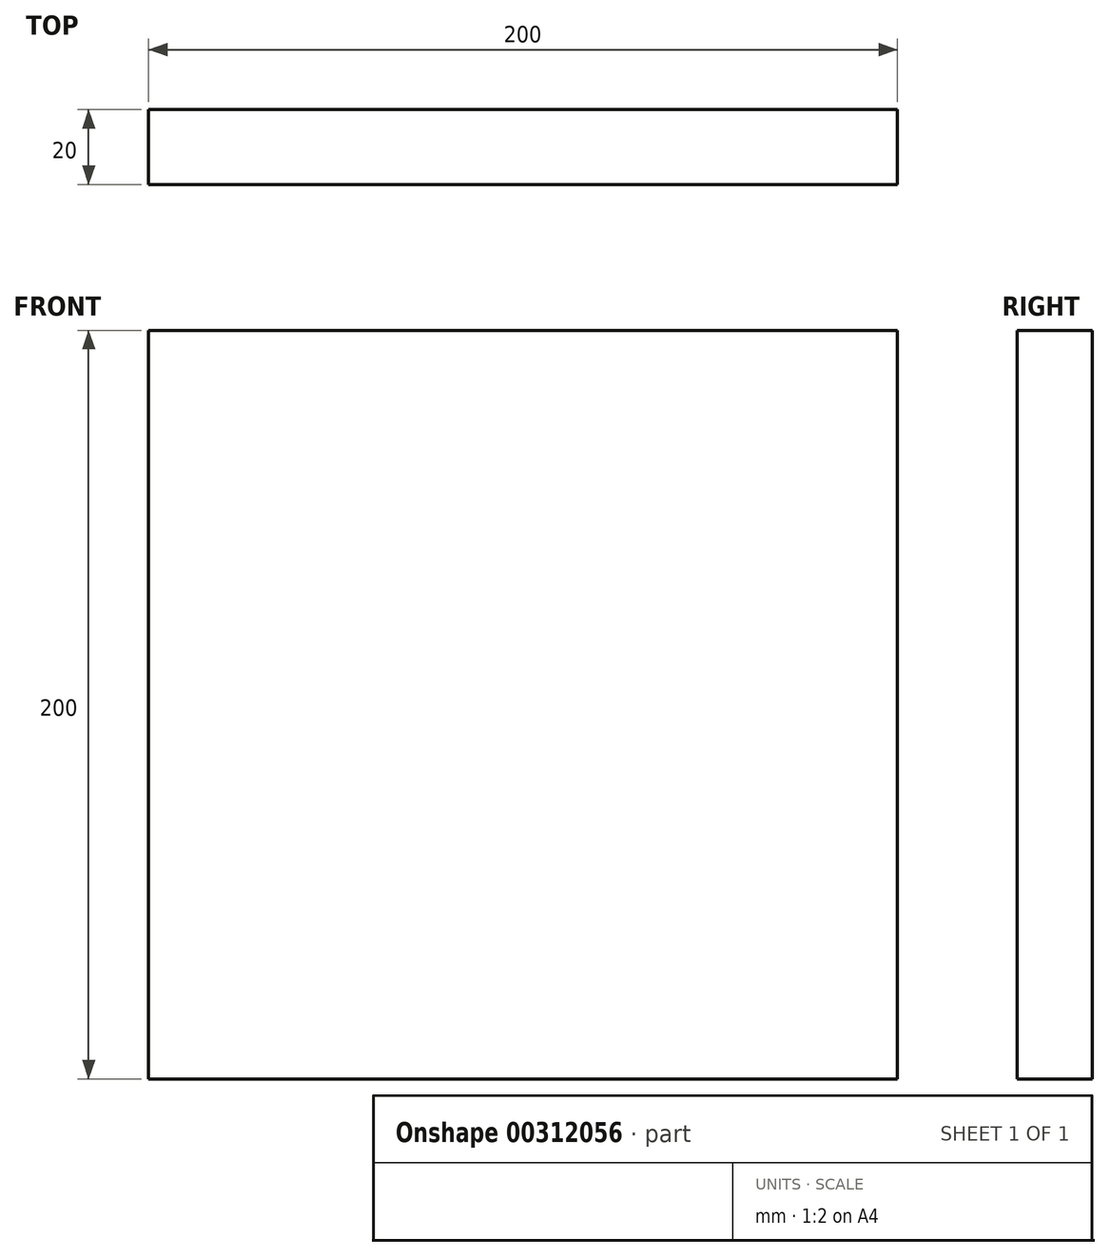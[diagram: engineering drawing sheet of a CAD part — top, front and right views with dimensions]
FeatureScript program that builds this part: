
annotation { "Feature Type Name" : "Feature", "Feature Type Description" : "" }
export const myFeature = defineFeature(function(context is Context, id is Id, definition is map)
    precondition{}
    {
        {
            var Q0;
            Q0=qCreatedBy(makeId("Front.planeOp"),FACE);
            var sketch = newSketch(context, id + "F0", { "sketchPlane" : qUnion([Q0])});
            skLineSegment(sketch, "E0.bottom", {"start": v(100, -100) * mm, "end": v(-100, -100) * mm});
            skLineSegment(sketch, "E0.top", {"start": v(100, 100) * mm, "end": v(-100, 100) * mm});
            skLineSegment(sketch, "E0.left", {"start": v(100, -100) * mm, "end": v(100, 100) * mm});
            skLineSegment(sketch, "E0.right", {"start": v(-100, -100) * mm, "end": v(-100, 100) * mm});
            skPoint(sketch, "E0.middle", {"position": v(0, 0) * mm});
            skSolve(sketch);
        }
        {
            var Q0;
            Q0 = qSketchRegion(id + "F0", true);
            extrude(context, id + "F1", {"entities" : qUnion([Q0]), "depth" : 20 * mm});
        }
    });
